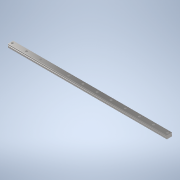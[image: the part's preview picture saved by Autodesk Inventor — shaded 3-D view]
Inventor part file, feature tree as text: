
AUTODESK INVENTOR PART (.ipt)
format: ipt  version: 2022.2 (Build 262287010, 287A)  size: 153,088 bytes
history: native  units: mm
features: chamfer x3, sketch x2, extrude x1, hole x1, pattern_linear x1
ambient origin geometry x8: Origin, YZ Plane, XZ Plane, XY Plane, X Axis, Y Axis, Z Axis, Center Point
bodies: Volumenkörper1 (feature_tree)
feature tree (8):
  extrude  "Extrusion1"  Depth=15.0mm
  chamfer  "Fase1"  Distance=3.5mm
  chamfer  "Fase2"  Distance=450.0mm
  chamfer  "Fase3"  Distance=0.4mm Angle=45.0deg
  hole  "Bohrung1"  [1 undecoded]
  pattern_linear  "Rechteckige Anordnung1"  Spacing1=0.4mm  [1 undecoded]
  sketch  "Skizze1"  dims[d1=1.5mm d2=15.0mm]
  sketch  "Skizze2"  dims[d3=10.0mm d4=3.5mm d5=450.0mm d6=0.0mm d7=0.4mm d8=0.4mm d9=45.0deg d10=0.4mm d11=0.4mm d12=45.0deg d13=0.4mm d14=0.4mm d15=45.0deg d16=5.0mm d17=3.4mm d18=6.0mm d19=6.0mm d20=4.9mm d21=90.0deg d22=8.0mm d23=20.594885mm d24=120.0mm d26=40.0mm]
note: 2 required parameter values undecoded (feature->parameter linkage not recoverable at this tier; creation-order binding heuristic only, values carry confidence <= 0.55)
